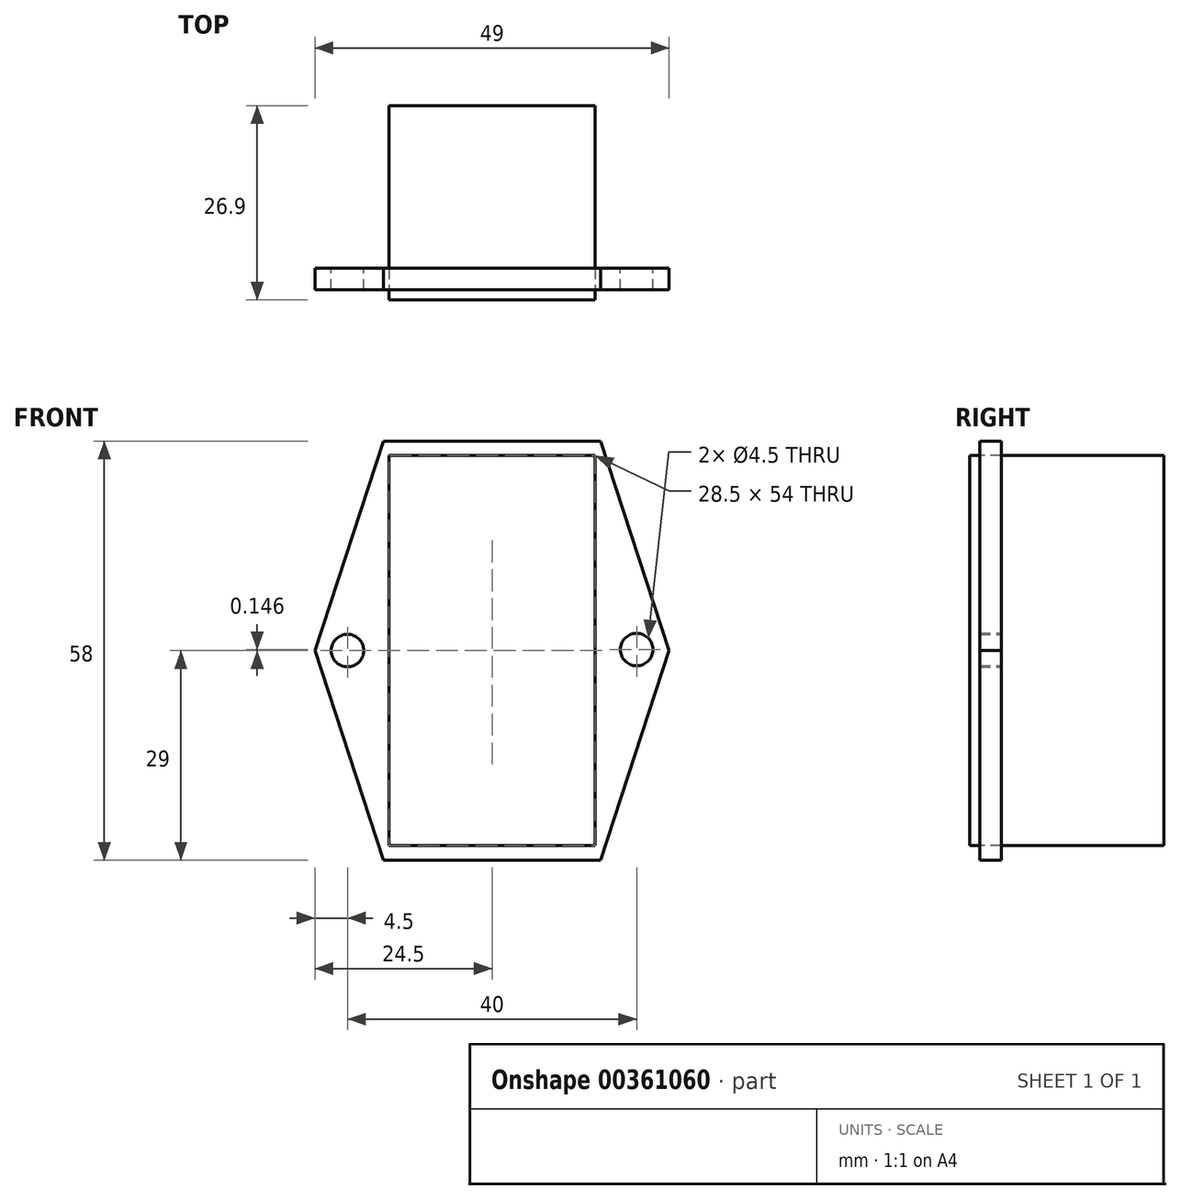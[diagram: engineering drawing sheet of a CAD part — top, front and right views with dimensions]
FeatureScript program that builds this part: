
annotation { "Feature Type Name" : "Feature", "Feature Type Description" : "" }
export const myFeature = defineFeature(function(context is Context, id is Id, definition is map)
    precondition{}
    {
        {
            var Q0;
            Q0=qCreatedBy(makeId("Front.planeOp"),FACE);
            var sketch = newSketch(context, id + "F0", { "sketchPlane" : qUnion([Q0])});
            skCircle(sketch, "E0", {"center": v(-20, 0) * mm, "radius": 2.25 * mm});
            skCircle(sketch, "E1", {"center": v(20, 0.15) * mm, "radius": 2.25 * mm});
            skPoint(sketch, "E2", {"position": v(-24.5, 0) * mm});
            skPoint(sketch, "E3", {"position": v(24.5, 0) * mm});
            skPoint(sketch, "E4", {"position": v(0, 29) * mm});
            skPoint(sketch, "E5", {"position": v(0, -29) * mm});
            skLineSegment(sketch, "E6", {"start": v(-15, 29) * mm, "end": v(15, 29) * mm});
            skLineSegment(sketch, "E7", {"start": v(-15, -29) * mm, "end": v(15, -29) * mm});
            skLineSegment(sketch, "E8", {"start": v(-15, 29) * mm, "end": v(-24.5, 0) * mm});
            skLineSegment(sketch, "E9", {"start": v(-15, -29) * mm, "end": v(-24.5, 0) * mm});
            skLineSegment(sketch, "E10", {"start": v(15, -29) * mm, "end": v(24.5, 0) * mm});
            skLineSegment(sketch, "E11", {"start": v(24.5, 0) * mm, "end": v(15, 29) * mm});
            skLineSegment(sketch, "E12", {"start": v(0, 27) * mm, "end": v(0, -27) * mm});
            skLineSegment(sketch, "E13", {"start": v(-14.25, 27) * mm, "end": v(14.25, 27) * mm});
            skLineSegment(sketch, "E14", {"start": v(-14.25, -27) * mm, "end": v(14.25, -27) * mm});
            skLineSegment(sketch, "E15", {"start": v(-14.25, 27) * mm, "end": v(-14.25, -27) * mm});
            skLineSegment(sketch, "E16", {"start": v(14.25, -27) * mm, "end": v(14.25, 27) * mm});
            skSolve(sketch);
        }
        {
            var Q0;
            Q0=makeQuery(id+"F0.imprint","IMPRINT",FACE,{"disambiguationData":[TD([[makeQuery(id+"F0.imprint","IMPRINT",EDGE,{"derivedFrom":sQuery(id+"F0.wireOp",EDGE,"E0")}),-1.0]])]});
            extrude(context, id + "F1", {"entities" : qUnion([Q0]), "depth" : 3 * mm});
        }
        {
            var Q0;
            {var subQ0=sQuery(id+"F0.wireOp",EDGE,"E12");Q0=makeQuery(id+"F0.imprint","IMPRINT",FACE,{"disambiguationData":[TD([[makeQuery(id+"F0.imprint","IMPRINT",EDGE,{"derivedFrom":subQ0}),-1.0]])]});}
            var Q1;
            {var subQ0=sQuery(id+"F0.wireOp",EDGE,"E12");Q1=makeQuery(id+"F0.imprint","IMPRINT",FACE,{"disambiguationData":[TD([[makeQuery(id+"F0.imprint","IMPRINT",EDGE,{"derivedFrom":subQ0}),1.0]])]});}
            extrude(context, id + "F2", {"entities" : qUnion([Q0, Q1]), "oppositeDirection" : true, "depth" : 22.5 * mm, "hasSecondDirection" : true, "secondDirectionOppositeDirection" : false, "secondDirectionDepth" : 4.4 * mm});
        }
    });
